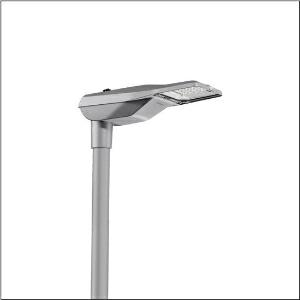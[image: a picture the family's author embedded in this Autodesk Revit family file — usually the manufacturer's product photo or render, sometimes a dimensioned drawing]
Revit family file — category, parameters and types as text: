
# Revit family: streetlight_sl_21_iq_micro___st1_0a_5xe1d31v08db_4967
name_source: partatom
category: Lighting Fixtures
units: mm (PartAtom-declared; Revit-internal decimal feet)

## family parameters
Cut with Voids When Loaded = No
Host = Face
Light Source = No
Part Type = Normal
Room Calculation Point = No
Round Connector Dimension = Use Diameter
Shared = No

## types (1)
- --- (1 x LED, 5110 lm, 39.1 W, 3000K)
    Apparent Load = 39 VA
    CIE Flux Codes = 37 72 97 100 100
    Color Rendering = 70
    Color Temperature = 3000K
    Default Elevation = 1800 mm
    Description = Streetlight SL 21 iQ micro, mast luminaire, primary light control with lens, of PMMA, primary optical cover: cover, of toughened safety glass, transparent, light distribution: ST1.0a, light emission: direct distribution, primary light characteristic: asymmetric, installation type: post-top, side-entry, LED, High Power LED, rated luminous flux: 5.110lm, luminous efficacy: 131lm/W, light colour: 730, colour temperature: 3000K, control: presetting dimming logarithmic, Street-Remote, Auto-Match, Temp-Guard, Lumen-Switch, Night-Set, Smart-Wire, Light-Fading, Desk-Remote (wireless, voltage-free reading and setting of iQ features in the workshop via application-optimized NFC function/RFID function), optimised constant luminous flux control (CLO 2.0), mains connection: 220..240V, AC, 50/60Hz, start of lifetime: 39W, end of service life: 41W, reduction: 17W, luminaire housing, of diecast aluminium, powder-coated, Siteco® metallic grey (DB 702S), corrosivity category C5 mid according to DIN EN ISO 12944, please order mast flange separately, inclination adjustable: 0°, 5°, 10°, 15°, sealing non-destructively replaceable, multi-level sealing system, length: 528mm, width: 235mm, height: 110mm, mast flange for spigot size: 42mm (side-entry): 5XC10008XM4, 60/48mm (side-entry/post-top): 5XC10108XM2, 76/60mm (side-entry/post-top): 5XC10108XM1, Smart Interface above, protection rating (complete): IP66, insulation class (complete): insulation class II (safety insulation), certification: CE, ENEC, ENEC+, VDE, impact resistance: IK09, permissible operating ambient temperature for outdoor applications: -40..+50°C, standard-compliant lighting for roads and squares, packaging unit: 1 piece

Light Distribution: ST1.0a
    Height = 110 mm
    Lamp = 1 x LED
    Lamp Light Flux = 5110 lm
    Lamp Power = 39.1 W
    Lamp count = 1
    Length = 528 mm
    Luminous efficacy = 131 lm/W
    Manufacturer = Siteco
    ModVariant = No
    Model = 5XE1D31V08DB
    Number of Poles = 1
    OnlyDefault = Yes
    Power Factor = 1
    Product Name = Streetlight SL 21 iQ micro | ST1.0a
    Product group = mast luminaire | pylon top
    ProductGroupID = 6100
    Protection Class = Protection class II
    Protection Degree = IP 66
    RLX_Detail_Level = 1
    RLX_Emergency_Light_Flux = 0 lm
    RLX_Emergency_Type = 0
    RLX_Emergency_Type_DB = No
    RlxData = <blob elided: 98469 chars, md5=5a07ec21>
    Socket = socket
    Standby Power = 0 W
    System Light Flux = 5110 lm
    System Power = 39 W
    Type Comments = factory setting: luminous flux: 100 % | dim-lin: 254 | 765 mA
    Type Image = l_1277292.jpg
    URL = http://relux.com
    VarID = @adj_045685
    Voltage = 0 V
    Weight = 0.00 kg
    Width = 235 mm

## geometry (parser evidence)
native form markers: Blend x4, Sweep x10
no freeform markers — native parametric forms only
